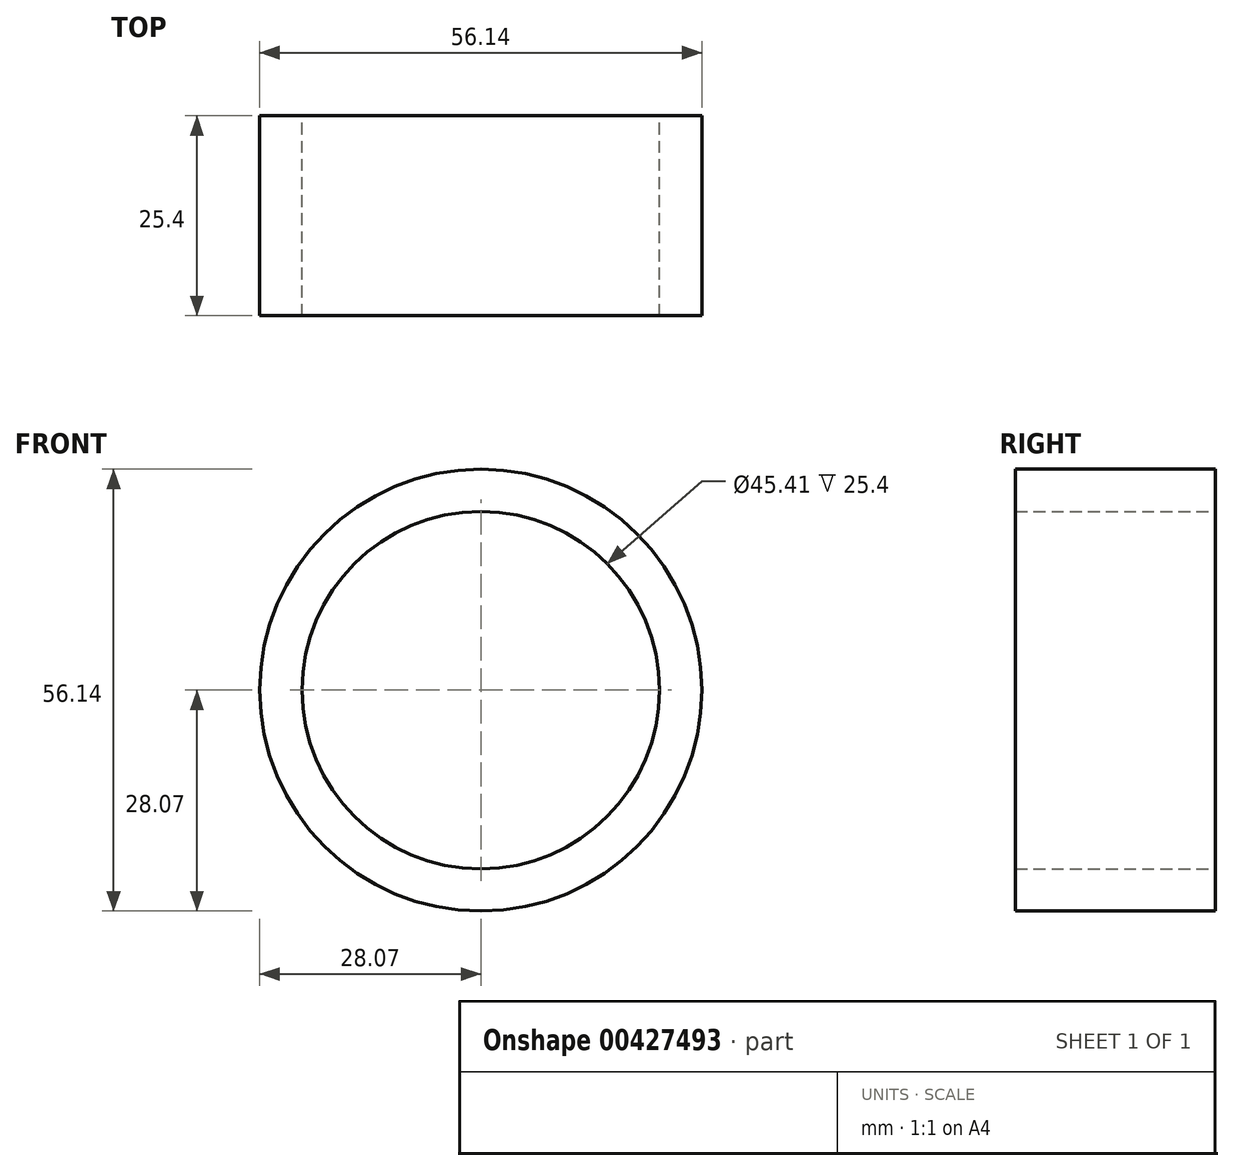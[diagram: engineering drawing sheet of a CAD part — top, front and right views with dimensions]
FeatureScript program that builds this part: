
annotation { "Feature Type Name" : "Feature", "Feature Type Description" : "" }
export const myFeature = defineFeature(function(context is Context, id is Id, definition is map)
    precondition{}
    {
        {
            var Q0;
            Q0=qCreatedBy(makeId("Front.planeOp"),FACE);
            var sketch = newSketch(context, id + "F0", { "sketchPlane" : qUnion([Q0])});
            skCircle(sketch, "E0", {"center": v(0, 0) * mm, "radius": 28.07 * mm});
            skCircle(sketch, "E1", {"center": v(0, 0) * mm, "radius": 22.7 * mm});
            skSolve(sketch);
        }
        {
            var Q0;
            Q0=makeQuery(id+"F0.imprint","IMPRINT",FACE,{"disambiguationData":[TD([[makeQuery(id+"F0.imprint","IMPRINT",EDGE,{"derivedFrom":sQuery(id+"F0.wireOp",EDGE,"E0")}),1.0]])]});
            extrude(context, id + "F1", {"entities" : qUnion([Q0]), "depth" : 25.4 * mm});
        }
    });
